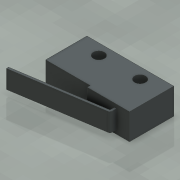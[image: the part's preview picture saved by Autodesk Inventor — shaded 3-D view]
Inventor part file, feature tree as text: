
AUTODESK INVENTOR PART (.ipt)
format: ipt  version: 2015 (Build 190159000, 159)  size: 118,272 bytes
history: native  units: mm
features: extrude x3, sketch x3
ambient origin geometry x8: Origin, YZ Plane, XZ Plane, XY Plane, X Axis, Y Axis, Z Axis, Center Point
bodies: Solid1 (feature_tree)
feature tree (6):
  extrude  "Extrusion1"  Depth=10.2mm
  extrude  "Extrusion2"  Depth=9.75mm
  extrude  "Extrusion3"  Depth=4.2mm
  sketch  "Sketch1"  dims[d0=20.0mm d2=10.2mm]
  sketch  "Sketch2"  dims[d3=9.5mm d4=9.75mm]
  sketch  "Sketch3"  dims[d5=9.5mm d6=2.54mm d7=2.5mm d8=6.0mm d9=0.0mm d10=4.2mm d11=0.5mm d12=3.0mm d13=1.0mm d14=0.0mm d15=0.5mm d17=4.2mm d18=0.0mm]
